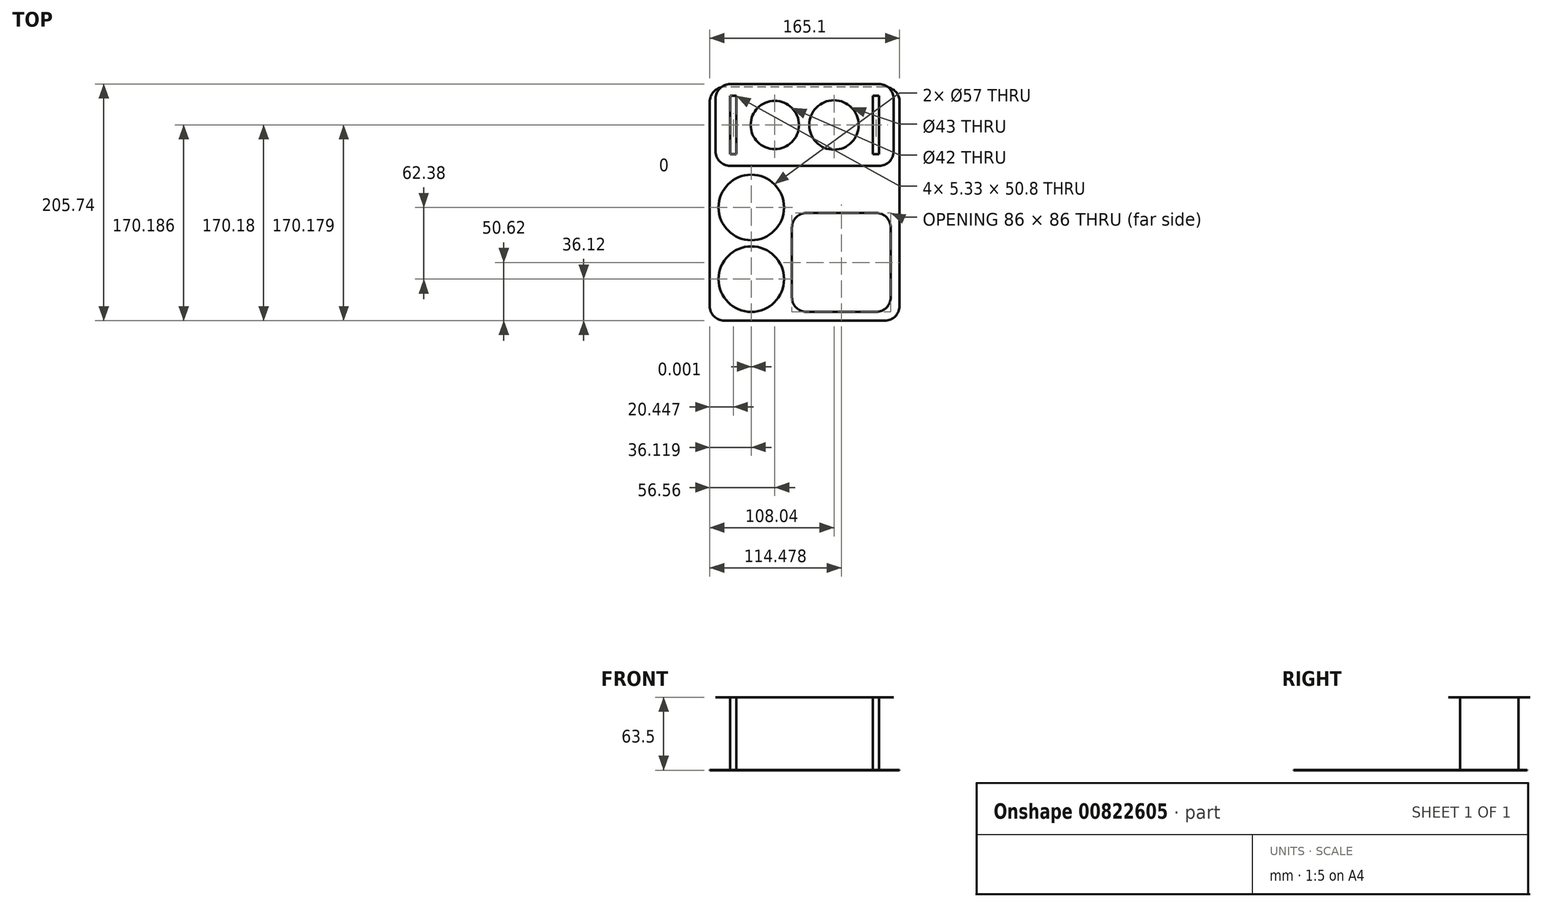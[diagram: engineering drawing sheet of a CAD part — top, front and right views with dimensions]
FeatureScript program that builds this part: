
annotation { "Feature Type Name" : "Feature", "Feature Type Description" : "" }
export const myFeature = defineFeature(function(context is Context, id is Id, definition is map)
    precondition{}
    {
        {
            assignVariable(context, id + "F0", {"name" : "Mat", "anyValue" : .21});
        }
        {
            var Q0;
            Q0=qCreatedBy(makeId("Top.planeOp"),FACE);
            var sketch = newSketch(context, id + "F1", { "sketchPlane" : qUnion([Q0])});
            skLineSegment(sketch, "E0.bottom", {"start": v(82.55, -101.6) * mm, "end": v(-82.55, -101.6) * mm});
            skLineSegment(sketch, "E0.top", {"start": v(82.55, 101.6) * mm, "end": v(-82.55, 101.6) * mm});
            skLineSegment(sketch, "E0.left", {"start": v(82.55, -101.6) * mm, "end": v(82.55, 101.6) * mm});
            skLineSegment(sketch, "E0.right", {"start": v(-82.55, -101.6) * mm, "end": v(-82.55, 101.6) * mm});
            skPoint(sketch, "E0.middle", {"position": v(0, 0) * mm});
            skCircle(sketch, "E1", {"center": v(-46.43, -65.48) * mm, "radius": 28.5 * mm});
            skLineSegment(sketch, "E2.bottom", {"start": v(74.93, -93.98) * mm, "end": v(-11.07, -93.98) * mm});
            skLineSegment(sketch, "E2.top", {"start": v(74.93, -7.98) * mm, "end": v(-11.07, -7.98) * mm});
            skLineSegment(sketch, "E2.left", {"start": v(74.93, -93.98) * mm, "end": v(74.93, -7.98) * mm});
            skLineSegment(sketch, "E2.right", {"start": v(-11.07, -93.98) * mm, "end": v(-11.07, -7.98) * mm});
            skPoint(sketch, "E2.middle", {"position": v(31.93, -50.98) * mm});
            skLineSegment(sketch, "E3.bottom", {"start": v(-59.44, 43.18) * mm, "end": v(-64.77, 43.18) * mm});
            skLineSegment(sketch, "E3.top", {"start": v(-59.44, 93.98) * mm, "end": v(-64.77, 93.98) * mm});
            skLineSegment(sketch, "E3.left", {"start": v(-59.44, 43.18) * mm, "end": v(-59.44, 93.98) * mm});
            skLineSegment(sketch, "E3.right", {"start": v(-64.77, 43.18) * mm, "end": v(-64.77, 93.98) * mm});
            skPoint(sketch, "E3.middle", {"position": v(-62.1, 68.58) * mm});
            skLineSegment(sketch, "E4.bottom", {"start": v(64.77, 43.18) * mm, "end": v(59.44, 43.18) * mm});
            skLineSegment(sketch, "E4.top", {"start": v(64.77, 93.98) * mm, "end": v(59.44, 93.98) * mm});
            skLineSegment(sketch, "E4.left", {"start": v(64.77, 43.18) * mm, "end": v(64.77, 93.98) * mm});
            skLineSegment(sketch, "E4.right", {"start": v(59.44, 43.18) * mm, "end": v(59.44, 93.98) * mm});
            skPoint(sketch, "E4.middle", {"position": v(62.1, 68.58) * mm});
            skPoint(sketch, "E4.middle.positionSnap0", {"position": v(-59.44, 68.58) * mm});
            skPoint(sketch, "E4.centerSnap0", {"position": v(-59.44, 68.58) * mm});
            skCircle(sketch, "E5", {"center": v(-46.43, -3.1) * mm, "radius": 28.5 * mm});
            skSolve(sketch);
        }
        {
            var Q0;
            Q0=makeQuery(id+"F1.imprint","IMPRINT",FACE,{"disambiguationData":[TD([[makeQuery(id+"F1.imprint","IMPRINT",EDGE,{"derivedFrom":sQuery(id+"F1.wireOp",EDGE,"E0.bottom")}),-1.0]])]});
            extrude(context, id + "F2", {"entities" : qUnion([Q0]), "depth" : (getVariable(context, 'Mat')) * mm, "offsetDistance" : 25.4 * mm});
        }
        {
            var Q0;
            Q0=makeQuery(id+"F2.opExtrude","CAP_FACE",FACE,{"disambiguationData":[OSD([sQuery(id+"F1.wireOp",EDGE,"E0.bottom"),sQuery(id+"F1.wireOp",EDGE,"E0.top"),sQuery(id+"F1.wireOp",EDGE,"E0.left"),sQuery(id+"F1.wireOp",EDGE,"E0.right"),sQuery(id+"F1.wireOp",EDGE,"E1"),sQuery(id+"F1.wireOp",EDGE,"E2.bottom"),sQuery(id+"F1.wireOp",EDGE,"E2.top"),sQuery(id+"F1.wireOp",EDGE,"E2.left"),sQuery(id+"F1.wireOp",EDGE,"E2.right"),sQuery(id+"F1.wireOp",EDGE,"E3.bottom"),sQuery(id+"F1.wireOp",EDGE,"E3.top"),sQuery(id+"F1.wireOp",EDGE,"E3.left"),sQuery(id+"F1.wireOp",EDGE,"E3.right"),sQuery(id+"F1.wireOp",EDGE,"E4.bottom"),sQuery(id+"F1.wireOp",EDGE,"E4.top"),sQuery(id+"F1.wireOp",EDGE,"E4.left"),sQuery(id+"F1.wireOp",EDGE,"E4.right"),sQuery(id+"F1.wireOp",EDGE,"E5")])],"isStart":true});
            var sketch = newSketch(context, id + "F3", { "sketchPlane" : qUnion([Q0])});
            skLineSegment(sketch, "E6.0", {"start": v(-59.44, -43.18) * mm, "end": v(-59.44, -93.98) * mm});
            skLineSegment(sketch, "E7.0", {"start": v(-64.77, -43.18) * mm, "end": v(-64.77, -93.98) * mm});
            skPoint(sketch, "E8.0", {"position": v(-62.1, -93.98) * mm});
            skLineSegment(sketch, "E9.0", {"start": v(-59.44, -93.98) * mm, "end": v(-64.77, -93.98) * mm});
            skPoint(sketch, "E10.0", {"position": v(-62.1, -43.18) * mm});
            skLineSegment(sketch, "E11.0", {"start": v(-59.44, -43.18) * mm, "end": v(-64.77, -43.18) * mm});
            skLineSegment(sketch, "E12.0", {"start": v(64.77, -43.18) * mm, "end": v(64.77, -93.98) * mm});
            skLineSegment(sketch, "E13.0", {"start": v(59.44, -43.18) * mm, "end": v(59.44, -93.98) * mm});
            skLineSegment(sketch, "E14.0", {"start": v(64.77, -43.18) * mm, "end": v(59.44, -43.18) * mm});
            skLineSegment(sketch, "E15.0", {"start": v(64.77, -93.98) * mm, "end": v(59.44, -93.98) * mm});
            skSolve(sketch);
        }
        {
            var Q0;
            Q0=qSketchRegion(id+"F3",true);
            extrude(context, id + "F4", {"entities" : qUnion([Q0]), "oppositeDirection" : true, "depth" : 63.5 * mm, "offsetDistance" : 25.4 * mm});
        }
        {
            var Q0;
            Q0=makeQuery(id+"F4.opExtrude","CAP_FACE",FACE,{"disambiguationData":[OSD([sQuery(id+"F3.wireOp",EDGE,"E6.0"),sQuery(id+"F3.wireOp",EDGE,"E7.0"),sQuery(id+"F3.wireOp",EDGE,"E9.0"),sQuery(id+"F3.wireOp",EDGE,"E11.0")])],"isStart":false});
            var sketch = newSketch(context, id + "F5", { "sketchPlane" : qUnion([Q0])});
            skLineSegment(sketch, "E16.bottom", {"start": v(-77.47, 104.14) * mm, "end": v(77.47, 104.14) * mm});
            skLineSegment(sketch, "E16.top", {"start": v(-77.47, 33.02) * mm, "end": v(77.47, 33.02) * mm});
            skLineSegment(sketch, "E16.left", {"start": v(-77.47, 104.14) * mm, "end": v(-77.47, 33.02) * mm});
            skLineSegment(sketch, "E16.right", {"start": v(77.47, 104.14) * mm, "end": v(77.47, 33.02) * mm});
            skCircle(sketch, "E17", {"center": v(25.49, 68.58) * mm, "radius": 21.5 * mm});
            skCircle(sketch, "E18", {"center": v(-26, 68.59) * mm, "radius": 21 * mm});
            skLineSegment(sketch, "E19.0.0", {"start": v(64.77, 93.98) * mm, "end": v(59.44, 93.98) * mm});
            skLineSegment(sketch, "E19.0.1", {"start": v(59.44, 93.98) * mm, "end": v(59.44, 43.18) * mm});
            skLineSegment(sketch, "E19.0.2", {"start": v(59.44, 43.18) * mm, "end": v(64.77, 43.18) * mm});
            skLineSegment(sketch, "E19.0.3", {"start": v(64.77, 43.18) * mm, "end": v(64.77, 93.98) * mm});
            skLineSegment(sketch, "E20.0.0", {"start": v(-59.44, 93.98) * mm, "end": v(-64.77, 93.98) * mm});
            skLineSegment(sketch, "E20.0.1", {"start": v(-64.77, 93.98) * mm, "end": v(-64.77, 43.18) * mm});
            skLineSegment(sketch, "E20.0.2", {"start": v(-64.77, 43.18) * mm, "end": v(-59.44, 43.18) * mm});
            skLineSegment(sketch, "E20.0.3", {"start": v(-59.44, 43.18) * mm, "end": v(-59.44, 93.98) * mm});
            skSolve(sketch);
        }
        {
            var Q0;
            Q0=makeQuery(id+"F5.imprint","IMPRINT",FACE,{"disambiguationData":[TD([[makeQuery(id+"F5.imprint","IMPRINT",EDGE,{"derivedFrom":sQuery(id+"F5.wireOp",EDGE,"E16.bottom")}),-1.0]])]});
            extrude(context, id + "F6", {"entities" : qUnion([Q0]), "oppositeDirection" : true, "depth" : (getVariable(context, 'Mat')) * mm, "offsetDistance" : 25.4 * mm});
        }
        {
            var Q0;
            Q0=makeQuery(id+"F2.opExtrude","SWEPT_EDGE",EDGE,{"disambiguationData":[OSD([sQuery(id+"F1.wireOp",EDGE,"E0.bottom"),sQuery(id+"F1.wireOp",EDGE,"E0.right")])]});
            var Q1;
            Q1=makeQuery(id+"F2.opExtrude","SWEPT_EDGE",EDGE,{"disambiguationData":[OSD([sQuery(id+"F1.wireOp",EDGE,"E0.bottom"),sQuery(id+"F1.wireOp",EDGE,"E0.left")])]});
            var Q2;
            Q2=makeQuery(id+"F2.opExtrude","SWEPT_EDGE",EDGE,{"disambiguationData":[OSD([sQuery(id+"F1.wireOp",EDGE,"E0.top"),sQuery(id+"F1.wireOp",EDGE,"E0.right")])]});
            var Q3;
            Q3=makeQuery(id+"F2.opExtrude","SWEPT_EDGE",EDGE,{"disambiguationData":[OSD([sQuery(id+"F1.wireOp",EDGE,"E0.top"),sQuery(id+"F1.wireOp",EDGE,"E0.left")])]});
            var Q4;
            Q4=makeQuery(id+"F2.opExtrude","SWEPT_EDGE",EDGE,{"disambiguationData":[OSD([sQuery(id+"F1.wireOp",EDGE,"E2.top"),sQuery(id+"F1.wireOp",EDGE,"E2.right")])]});
            var Q5;
            Q5=makeQuery(id+"F2.opExtrude","SWEPT_EDGE",EDGE,{"disambiguationData":[OSD([sQuery(id+"F1.wireOp",EDGE,"E2.top"),sQuery(id+"F1.wireOp",EDGE,"E2.left")])]});
            var Q6;
            Q6=makeQuery(id+"F2.opExtrude","SWEPT_EDGE",EDGE,{"disambiguationData":[OSD([sQuery(id+"F1.wireOp",EDGE,"E2.bottom"),sQuery(id+"F1.wireOp",EDGE,"E2.left")])]});
            var Q7;
            Q7=makeQuery(id+"F2.opExtrude","SWEPT_EDGE",EDGE,{"disambiguationData":[OSD([sQuery(id+"F1.wireOp",EDGE,"E2.bottom"),sQuery(id+"F1.wireOp",EDGE,"E2.right")])]});
            var Q8;
            Q8=makeQuery(id+"F6.opExtrude","SWEPT_EDGE",EDGE,{"disambiguationData":[OSD([sQuery(id+"F5.wireOp",EDGE,"E16.top"),sQuery(id+"F5.wireOp",EDGE,"E16.left")])]});
            var Q9;
            Q9=makeQuery(id+"F6.opExtrude","SWEPT_EDGE",EDGE,{"disambiguationData":[OSD([sQuery(id+"F5.wireOp",EDGE,"E16.bottom"),sQuery(id+"F5.wireOp",EDGE,"E16.left")])]});
            var Q10;
            Q10=makeQuery(id+"F6.opExtrude","SWEPT_EDGE",EDGE,{"disambiguationData":[OSD([sQuery(id+"F5.wireOp",EDGE,"E16.top"),sQuery(id+"F5.wireOp",EDGE,"E16.right")])]});
            var Q11;
            Q11=makeQuery(id+"F6.opExtrude","SWEPT_EDGE",EDGE,{"disambiguationData":[OSD([sQuery(id+"F5.wireOp",EDGE,"E16.bottom"),sQuery(id+"F5.wireOp",EDGE,"E16.right")])]});
            fillet(context, id + "F7", {"entities" : qUnion([Q0, Q1, Q2, Q3, Q4, Q5, Q6, Q7, Q8, Q9, Q10, Q11]), "radius" : 12.7 * mm, "tangentPropagation" : true, "allowEdgeOverflow" : false});
        }
    });
